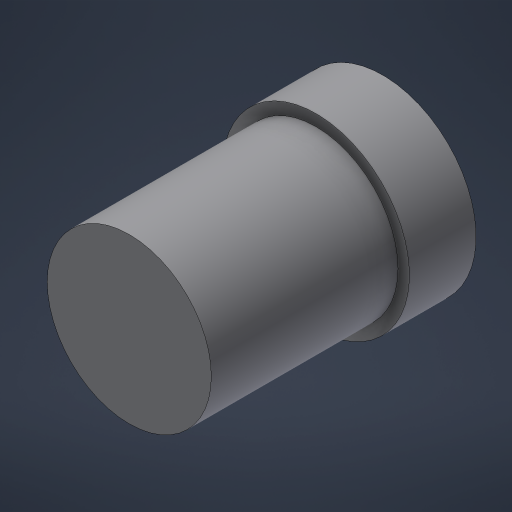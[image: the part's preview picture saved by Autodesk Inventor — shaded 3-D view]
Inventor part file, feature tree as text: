
AUTODESK INVENTOR PART (.ipt)
format: ipt  version: 2023.5 (Build 275446000, 446)  size: 397,312 bytes
history: native  units: mm
features: revolve x1, sketch x1
ambient origin geometry x8: Origin, YZ Plane, XZ Plane, XY Plane, X Axis, Y Axis, Z Axis, Center Point
bodies: Volumenkörper1 (feature_tree)
feature tree (2):
  revolve  "Umdrehung1"
  sketch  "Skizze1"  dims[d0=12.3mm d1=14.0mm d2=14.0mm d3=5.0mm d4=90.0deg]
